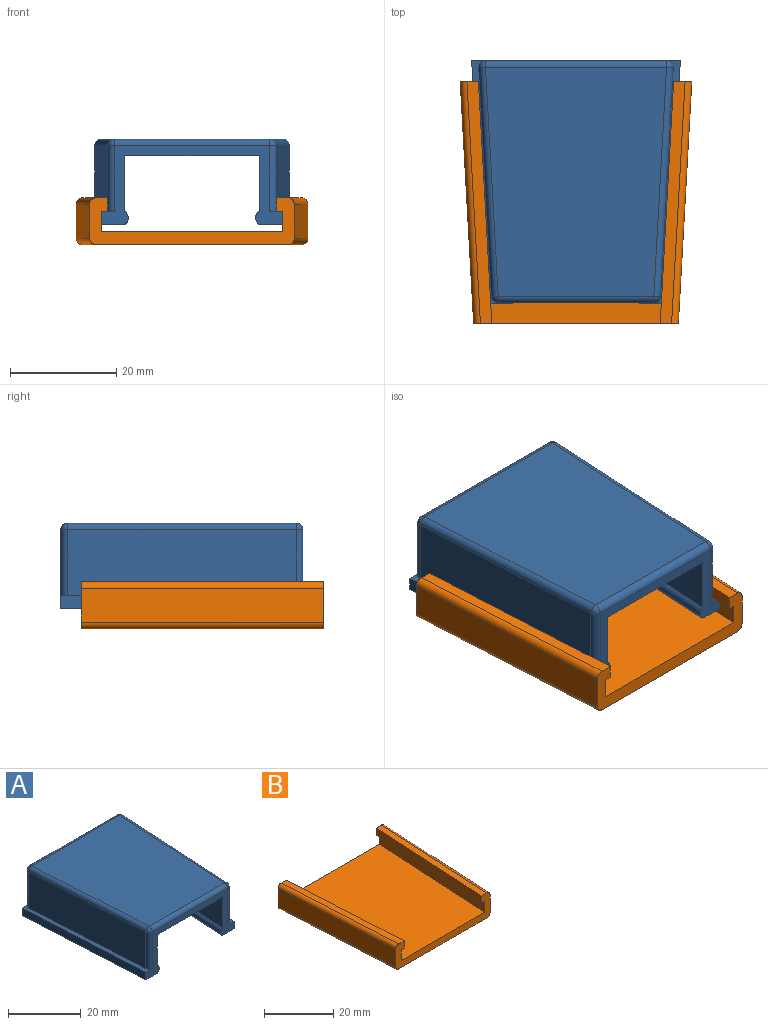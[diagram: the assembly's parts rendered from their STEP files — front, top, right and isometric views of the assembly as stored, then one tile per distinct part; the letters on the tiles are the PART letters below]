
ASSEMBLY  parts=2 mates=1
PART A: 28 faces, bbox 39.4x45.7x16.1 mm
  f0: plane 34.29x14.86mm, normal (0,-1,0), area 122mm2, adj f3,f4,f5,f6,f7,f8,f9,f10
  f1: plane 39.37x14.86mm, normal (0,1,0), area 128.2mm2, adj f3,f4,f5,f6,f7,f8,f9,f10
  f2: plane 43.18x12.32mm, normal (1,-0.06,0), area 532.8mm2, adj f3,f17,f23,f24
  f3: plane 45.72x5.01mm, normal (0,0,1), area 58.8mm2, adj f0,f1,f2,f4,f17,f23
  f4: plane 45.72x2.54mm, normal (1,-0.06,0), area 116.3mm2, adj f0,f1,f3,f5
  f5: plane 45.72x6.99mm, normal (0,0,-1), area 203.2mm2, adj f0,f1,f4,f6
  f6: bspline ~45.72x3.22mm, area 137.4mm2, adj f0,f1,f5,f7
  f7: plane 45.72x10.41mm, normal (-1,0.06,0), area 476.9mm2, adj f0,f1,f6,f8
  f8: plane 45.72x30.48mm, normal (0,0,-1), area 1277.4mm2, adj f0,f1,f7,f9
  f9: plane 45.72x10.41mm, normal (1,0.06,0), area 476.9mm2, adj f0,f1,f8,f10
  f10: bspline ~45.72x3.22mm, area 137.4mm2, adj f0,f1,f9,f11
  f11: plane 45.72x6.99mm, normal (0,0,-1), area 203.2mm2, adj f0,f1,f10,f12
  f12: plane 45.72x2.54mm, normal (-1,-0.06,0), area 116.3mm2, adj f0,f1,f11,f13
  f13: plane 45.72x5.01mm, normal (0,0,1), area 58.8mm2, adj f0,f1,f12,f14,f16,f22
  f14: plane 43.18x12.32mm, normal (-1,-0.06,0), area 532.8mm2, adj f13,f16,f21,f22
  f15: plane 43.18x34.15mm, normal (0,0,1), area 1370.8mm2, adj f18,f21,f24,f27
  f16: cylinder r=1.27mm len=12.32mm, axis (0,0,-1), area 23.7mm2, adj f0,f13,f14,f19
  f17: cylinder r=1.27mm len=12.32mm, axis (0,0,-1), area 23.7mm2, adj f0,f2,f3,f20
  f18: cylinder r=1.27mm len=29.35mm, axis (-1,0,0), area 58.5mm2, adj f0,f15,f19,f20
  f19: sphere r=1.27mm, area 2.4mm2, adj f16,f18,f21
  f20: sphere r=1.27mm, area 2.4mm2, adj f17,f18,f24
  f21: cylinder r=1.27mm len=43.25mm, axis (-0.06,1,0), area 86.3mm2, adj f14,f15,f19,f25
  f22: cylinder r=1.27mm len=12.32mm, axis (0,0,1), area 25.4mm2, adj f1,f13,f14,f25
  f23: cylinder r=1.27mm len=12.32mm, axis (0,0,1), area 25.4mm2, adj f1,f2,f3,f26
  f24: cylinder r=1.27mm len=43.25mm, axis (-0.06,-1,0), area 86.3mm2, adj f2,f15,f20,f26
  f25: sphere r=1.27mm, area 2.6mm2, adj f21,f22,f27
  f26: sphere r=1.27mm, area 2.6mm2, adj f23,f24,f27
  f27: cylinder r=1.27mm len=34.15mm, axis (1,0,0), area 68.1mm2, adj f1,f15,f25,f26
PART B: 18 faces, bbox 43.7x45.9x8.9 mm
  f0: plane 38.61x8.89mm, normal (0,-1,0), area 130.5mm2, adj f2,f3,f4,f5,f6,f7,f8,f9
  f1: plane 43.69x8.89mm, normal (0,1,0), area 143.5mm2, adj f2,f3,f4,f5,f6,f7,f8,f9
  f2: plane 45.72x3.81mm, normal (-1,0.06,0), area 174.5mm2, adj f0,f1,f3,f13
  f3: plane 45.72x3.81mm, normal (0,0,-1), area 58.1mm2, adj f0,f1,f2,f4
  f4: plane 45.72x2.54mm, normal (-1,0.06,0), area 116.3mm2, adj f0,f1,f3,f5
  f5: plane 45.72x4.7mm, normal (0,0,1), area 98.6mm2, adj f0,f1,f4,f17
  f6: plane 45.72x6.35mm, normal (1,-0.06,0), area 290.8mm2, adj f0,f1,f16,f17
  f7: plane 45.72x41.14mm, normal (0,0,-1), area 1765mm2, adj f0,f1,f15,f16
  f8: plane 45.72x6.35mm, normal (-1,-0.06,0), area 290.8mm2, adj f0,f1,f14,f15
  f9: plane 45.72x4.7mm, normal (0,0,1), area 98.6mm2, adj f0,f1,f10,f14
  f10: plane 45.72x2.54mm, normal (1,0.06,0), area 116.3mm2, adj f0,f1,f9,f11
  f11: plane 45.72x3.81mm, normal (0,0,-1), area 58.1mm2, adj f0,f1,f10,f12
  f12: plane 45.72x3.81mm, normal (1,0.06,0), area 174.5mm2, adj f0,f1,f11,f13
  f13: plane 45.72x39.37mm, normal (0,0,1), area 1683.9mm2, adj f0,f1,f2,f12
  f14: cylinder r=1.27mm len=45.86mm, axis (-0.06,1,0), area 91.3mm2, adj f0,f1,f8,f9
  f15: cylinder r=1.27mm len=45.86mm, axis (0.06,-1,0), area 91.3mm2, adj f0,f1,f7,f8
  f16: cylinder r=1.27mm len=45.86mm, axis (0.06,1,0), area 91.3mm2, adj f0,f1,f6,f7
  f17: cylinder r=1.27mm len=45.86mm, axis (0.06,1,0), area 91.3mm2, adj f0,f1,f5,f6
PLACE A t=(-17.15,0,0)mm
PLACE B t=(-17.15,-3.85,-1.27)mm
MATE slider B.f0 <-> A.f0  axis (0,-1,0) through (0,-3.85,2.54)mm
